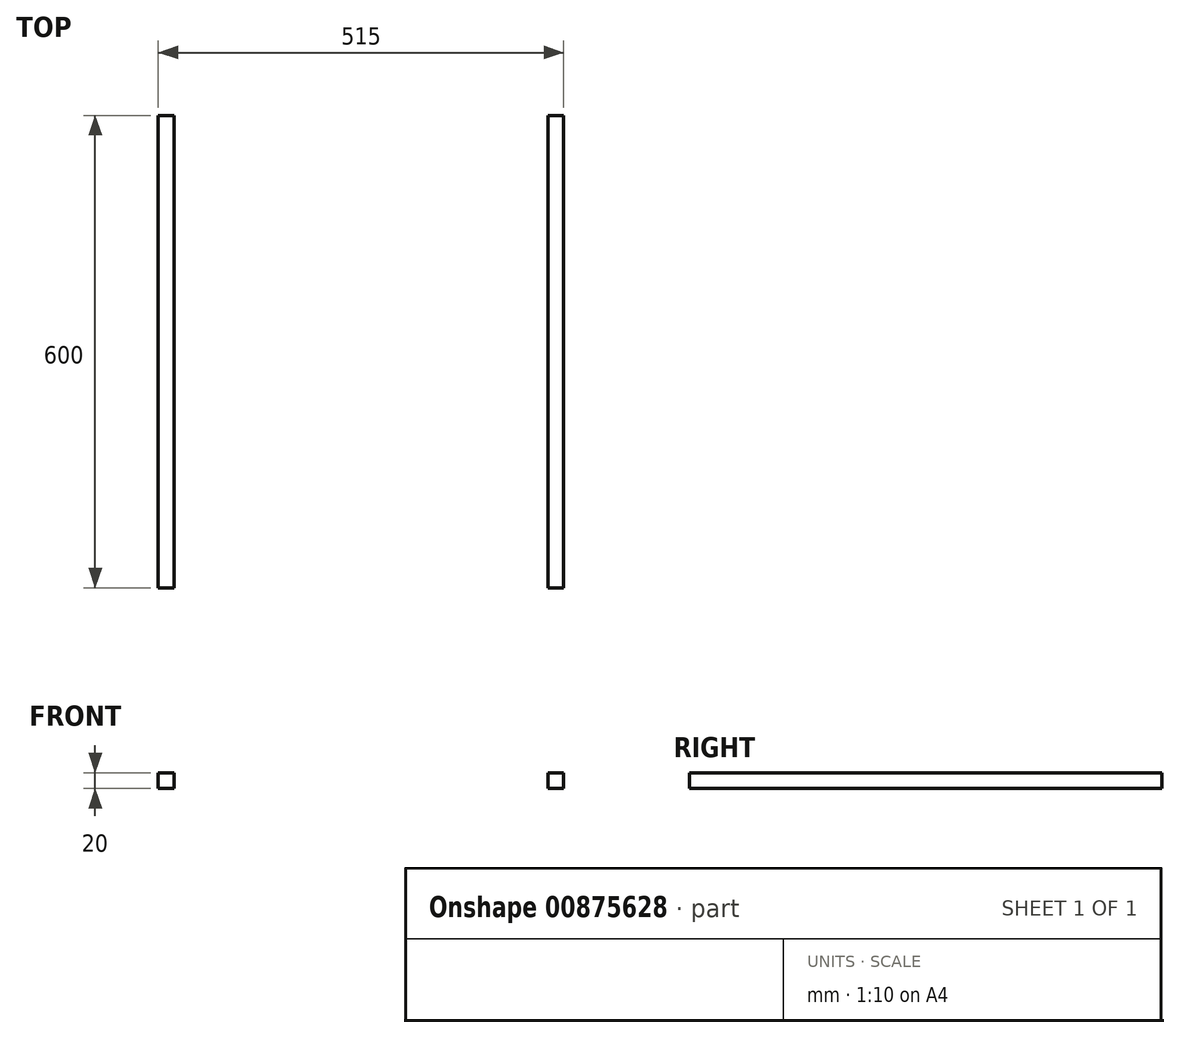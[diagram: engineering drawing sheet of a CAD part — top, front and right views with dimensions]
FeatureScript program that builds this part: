
annotation { "Feature Type Name" : "Feature", "Feature Type Description" : "" }
export const myFeature = defineFeature(function(context is Context, id is Id, definition is map)
    precondition{}
    {
        {
            var Q0;
            Q0=qCreatedBy(makeId("Top.planeOp"),FACE);
            var sketch = newSketch(context, id + "F0", { "sketchPlane" : qUnion([Q0])});
            skLineSegment(sketch, "E0.bottom", {"start": v(-81.87, 519.27) * mm, "end": v(-61.87, 519.27) * mm});
            skLineSegment(sketch, "E0.top", {"start": v(-81.87, -80.73) * mm, "end": v(-61.87, -80.73) * mm});
            skLineSegment(sketch, "E0.left", {"start": v(-81.87, 519.27) * mm, "end": v(-81.87, -80.73) * mm});
            skLineSegment(sketch, "E0.right", {"start": v(-61.87, 519.27) * mm, "end": v(-61.87, -80.73) * mm});
            skLineSegment(sketch, "E1.bottom", {"start": v(413.13, 519.27) * mm, "end": v(433.13, 519.27) * mm});
            skLineSegment(sketch, "E1.top", {"start": v(413.13, -80.73) * mm, "end": v(433.13, -80.73) * mm});
            skLineSegment(sketch, "E1.left", {"start": v(413.13, 519.27) * mm, "end": v(413.13, -80.73) * mm});
            skLineSegment(sketch, "E1.right", {"start": v(433.13, 519.27) * mm, "end": v(433.13, -80.73) * mm});
            skSolve(sketch);
        }
        {
            var Q0;
            Q0=makeQuery(id+"F0.imprint","IMPRINT",FACE,{"disambiguationData":[TD([[makeQuery(id+"F0.imprint","IMPRINT",EDGE,{"derivedFrom":sQuery(id+"F0.wireOp",EDGE,"E0.bottom")}),-1.0]])]});
            var Q1;
            Q1=makeQuery(id+"F0.imprint","IMPRINT",FACE,{"disambiguationData":[TD([[makeQuery(id+"F0.imprint","IMPRINT",EDGE,{"derivedFrom":sQuery(id+"F0.wireOp",EDGE,"E1.bottom")}),-1.0]])]});
            extrude(context, id + "F1", {"entities" : qUnion([Q0, Q1]), "depth" : 20 * mm, "offsetDistance" : 25 * mm});
        }
    });
